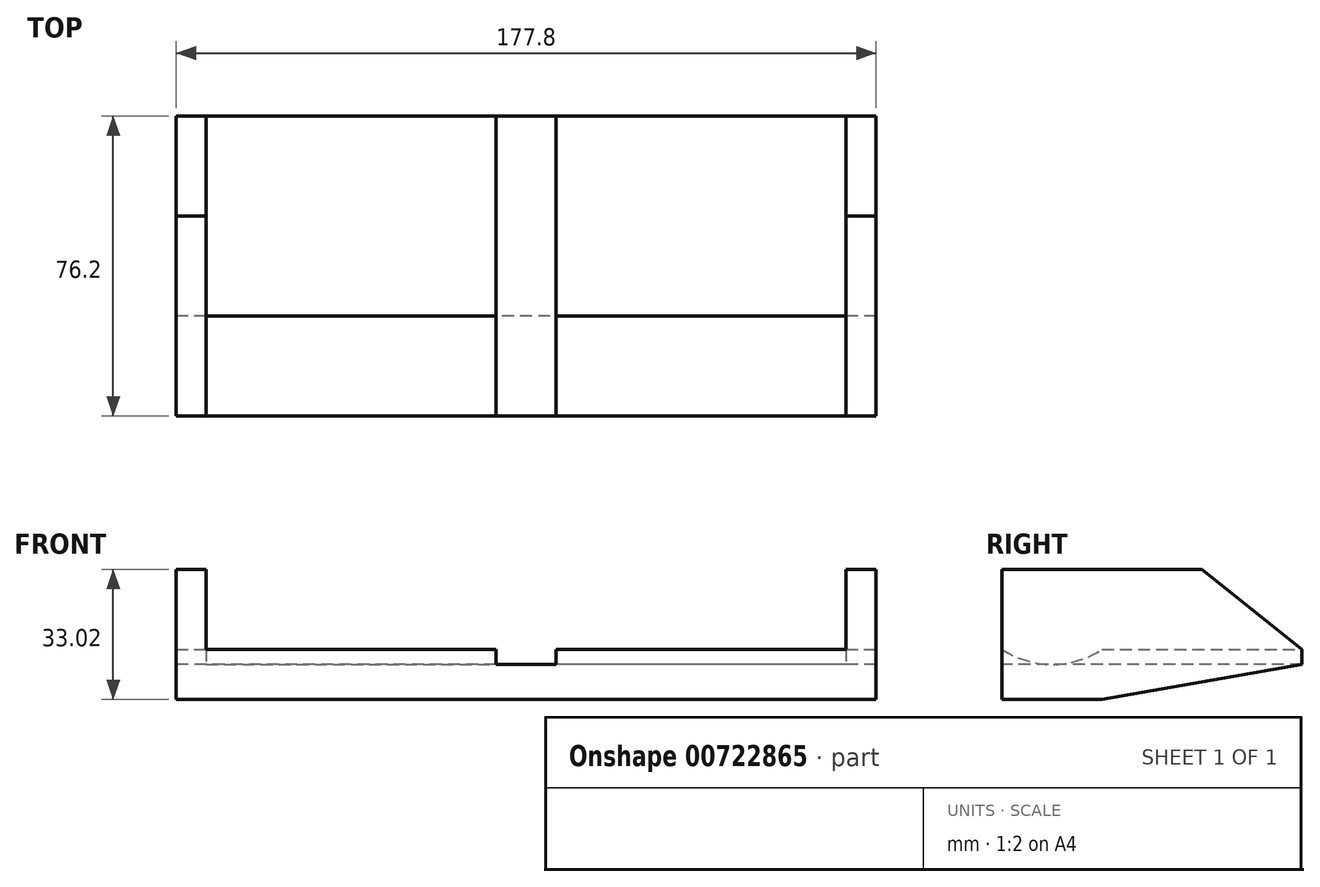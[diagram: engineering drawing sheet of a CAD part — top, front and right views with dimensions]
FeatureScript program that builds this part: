
annotation { "Feature Type Name" : "Feature", "Feature Type Description" : "" }
export const myFeature = defineFeature(function(context is Context, id is Id, definition is map)
    precondition{}
    {
        {
            var Q0;
            Q0=qCreatedBy(makeId("Top.planeOp"),FACE);
            var sketch = newSketch(context, id + "F0", { "sketchPlane" : qUnion([Q0])});
            skLineSegment(sketch, "E0.bottom", {"start": v(88.9, -38.1) * mm, "end": v(-88.9, -38.1) * mm});
            skLineSegment(sketch, "E0.top", {"start": v(88.9, 38.1) * mm, "end": v(-88.9, 38.1) * mm});
            skLineSegment(sketch, "E0.left", {"start": v(88.9, -38.1) * mm, "end": v(88.9, 38.1) * mm});
            skLineSegment(sketch, "E0.right", {"start": v(-88.9, -38.1) * mm, "end": v(-88.9, 38.1) * mm});
            skPoint(sketch, "E0.middle", {"position": v(0, 0) * mm});
            skSolve(sketch);
        }
        {
            var Q0;
            Q0=makeQuery(id+"F0.imprint","IMPRINT",FACE,{"disambiguationData":[TD([[makeQuery(id+"F0.imprint","IMPRINT",EDGE,{"derivedFrom":sQuery(id+"F0.wireOp",EDGE,"E0.bottom")}),-1.0]])]});
            extrude(context, id + "F1", {"entities" : qUnion([Q0]), "depth" : 12.7 * mm, "offsetDistance" : 25.4 * mm});
        }
        {
            var Q0;
            Q0=makeQuery(id+"F1.opExtrude","SWEPT_FACE",FACE,{"disambiguationData":[OSD([sQuery(id+"F0.wireOp",EDGE,"E0.bottom")])]});
            var sketch = newSketch(context, id + "F2", { "sketchPlane" : qUnion([Q0])});
            skLineSegment(sketch, "E1", {"start": v(0, 0) * mm, "end": v(0, 8.9) * mm});
            skLineSegment(sketch, "E2", {"start": v(0, 8.9) * mm, "end": v(7.62, 8.9) * mm});
            skLineSegment(sketch, "E3", {"start": v(7.62, 8.9) * mm, "end": v(-7.62, 8.9) * mm});
            skLineSegment(sketch, "E4", {"start": v(-7.62, 8.9) * mm, "end": v(-7.62, 12.7) * mm});
            skLineSegment(sketch, "E5", {"start": v(7.62, 8.9) * mm, "end": v(7.62, 12.7) * mm});
            skSolve(sketch);
        }
        {
            var Q0;
            {var subQ1=sQuery(id+"F2.wireOp",EDGE,"E4");Q0=makeQuery(id+"F2.imprint","IMPRINT",FACE,{"disambiguationData":[TD([[makeQuery(id+"F2.imprint","IMPRINT",EDGE,{"derivedFrom":subQ1}),-1.0]])]});}
            extrude(context, id + "F3", {"entities" : qUnion([Q0]), "operationType" : NewBodyOperationType.REMOVE, "oppositeDirection" : true, "depth" : 197.61 * mm, "offsetDistance" : 25.4 * mm});
        }
        {
            var Q0;
            {var subQ0=sQuery(id+"F0.wireOp",EDGE,"E0.bottom");var subQ1=sQuery(id+"F0.wireOp",EDGE,"E0.right");var subQ2=sQuery(id+"F0.wireOp",EDGE,"E0.top");Q0=makeQuery(id+"F3.boolean.opBoolean","SPLIT",FACE,{"disambiguationData":[TD([makeQuery(id+"F1.opExtrude","SWEPT_FACE",FACE,{"disambiguationData":[OSD([subQ1])]})])],"derivedFrom":makeQuery(id+"F1.opExtrude","CAP_FACE",FACE,{"disambiguationData":[OSD([subQ0,subQ2,sQuery(id+"F0.wireOp",EDGE,"E0.left"),subQ1])],"isStart":false})});}
            var sketch = newSketch(context, id + "F4", { "sketchPlane" : qUnion([Q0])});
            skLineSegment(sketch, "E6.bottom", {"start": v(-88.9, -38.1) * mm, "end": v(-81.28, -38.1) * mm});
            skLineSegment(sketch, "E6.top", {"start": v(-88.9, 38.1) * mm, "end": v(-81.28, 38.1) * mm});
            skLineSegment(sketch, "E6.left", {"start": v(-88.9, -38.1) * mm, "end": v(-88.9, 38.1) * mm});
            skLineSegment(sketch, "E6.right", {"start": v(-81.28, -38.1) * mm, "end": v(-81.28, 38.1) * mm});
            skSolve(sketch);
        }
        {
            var Q0;
            Q0=makeQuery(id+"F4.imprint","IMPRINT",FACE,{"disambiguationData":[TD([[makeQuery(id+"F4.imprint","IMPRINT",EDGE,{"derivedFrom":sQuery(id+"F4.wireOp",EDGE,"E6.bottom")}),-1.0]])]});
            extrude(context, id + "F5", {"entities" : qUnion([Q0]), "operationType" : NewBodyOperationType.ADD, "depth" : 20.32 * mm, "offsetDistance" : 25.4 * mm});
        }
        {
            var Q0;
            {var subQ0=sQuery(id+"F0.wireOp",EDGE,"E0.bottom");var subQ1=sQuery(id+"F0.wireOp",EDGE,"E0.top");var subQ2=sQuery(id+"F0.wireOp",EDGE,"E0.left");Q0=makeQuery(id+"F3.boolean.opBoolean","SPLIT",FACE,{"disambiguationData":[TD([makeQuery(id+"F1.opExtrude","SWEPT_FACE",FACE,{"disambiguationData":[OSD([subQ2])]})])],"derivedFrom":makeQuery(id+"F1.opExtrude","CAP_FACE",FACE,{"disambiguationData":[OSD([subQ0,subQ1,subQ2,sQuery(id+"F0.wireOp",EDGE,"E0.right")])],"isStart":false})});}
            var sketch = newSketch(context, id + "F6", { "sketchPlane" : qUnion([Q0])});
            skLineSegment(sketch, "E7.bottom", {"start": v(88.9, -38.1) * mm, "end": v(81.28, -38.1) * mm});
            skLineSegment(sketch, "E7.top", {"start": v(88.9, 38.1) * mm, "end": v(81.28, 38.1) * mm});
            skLineSegment(sketch, "E7.left", {"start": v(88.9, -38.1) * mm, "end": v(88.9, 38.1) * mm});
            skLineSegment(sketch, "E7.right", {"start": v(81.28, -38.1) * mm, "end": v(81.28, 38.1) * mm});
            skSolve(sketch);
        }
        {
            var Q0;
            Q0=makeQuery(id+"F6.imprint","IMPRINT",FACE,{"disambiguationData":[TD([[makeQuery(id+"F6.imprint","IMPRINT",EDGE,{"derivedFrom":sQuery(id+"F6.wireOp",EDGE,"E7.bottom")}),-1.0]])]});
            extrude(context, id + "F7", {"entities" : qUnion([Q0]), "operationType" : NewBodyOperationType.ADD, "depth" : 20.32 * mm, "offsetDistance" : 25.4 * mm});
        }
        {
            var Q0;
            Q0=makeQuery(id+"F3.boolean.opBoolean","COPY",FACE,{"derivedFrom":makeQuery(id+"F3.opExtrude","SWEPT_FACE",FACE,{"disambiguationData":[OSD([sQuery(id+"F2.wireOp",EDGE,"E4")])]})});
            var sketch = newSketch(context, id + "F8", { "sketchPlane" : qUnion([Q0])});
            skLineSegment(sketch, "E8", {"start": v(-38.1, 12.7) * mm, "end": v(-12.7, 12.7) * mm});
            skArc(sketch, "E9", {"start": v(-38.1, 12.7) * mm, "mid": v(-25.4, 8.9) * mm, "end": v(-12.7, 12.7) * mm});
            skSolve(sketch);
        }
        {
            var Q0;
            {var subQ0=sQuery(id+"F8.wireOp",EDGE,"E8");Q0=makeQuery(id+"F8.imprint","IMPRINT",FACE,{"disambiguationData":[TD([[makeQuery(id+"F8.imprint","IMPRINT",EDGE,{"derivedFrom":subQ0}),1.0]])]});}
            extrude(context, id + "F9", {"entities" : qUnion([Q0]), "operationType" : NewBodyOperationType.REMOVE, "oppositeDirection" : true, "depth" : 73.66 * mm, "offsetDistance" : 25.4 * mm});
        }
        {
            var Q0;
            Q0=makeQuery(id+"F3.boolean.opBoolean","COPY",FACE,{"derivedFrom":makeQuery(id+"F3.opExtrude","SWEPT_FACE",FACE,{"disambiguationData":[OSD([sQuery(id+"F2.wireOp",EDGE,"E5")])]})});
            var sketch = newSketch(context, id + "F10", { "sketchPlane" : qUnion([Q0])});
            skLineSegment(sketch, "E10", {"start": v(38.1, 12.7) * mm, "end": v(12.7, 12.7) * mm});
            skArc(sketch, "E11", {"start": v(12.7, 12.7) * mm, "mid": v(25.4, 8.9) * mm, "end": v(38.1, 12.7) * mm});
            skSolve(sketch);
        }
        {
            var Q0;
            Q0=makeQuery(id+"F10.imprint","IMPRINT",FACE,{"disambiguationData":[TD([[makeQuery(id+"F10.imprint","IMPRINT",EDGE,{"derivedFrom":sQuery(id+"F10.wireOp",EDGE,"E10")}),-1.0]])]});
            extrude(context, id + "F11", {"entities" : qUnion([Q0]), "operationType" : NewBodyOperationType.REMOVE, "oppositeDirection" : true, "depth" : 73.66 * mm, "offsetDistance" : 25.4 * mm});
        }
        {
            var Q0;
            Q0=makeQuery(id+"F5.boolean.opBoolean","MERGE",FACE,{"derivedFrom":[makeQuery(id+"F1.opExtrude","SWEPT_FACE",FACE,{"disambiguationData":[OSD([sQuery(id+"F0.wireOp",EDGE,"E0.right")])]}),makeQuery(id+"F5.opExtrude","SWEPT_FACE",FACE,{"disambiguationData":[OSD([sQuery(id+"F4.wireOp",EDGE,"E6.left")])]})]});
            var sketch = newSketch(context, id + "F12", { "sketchPlane" : qUnion([Q0])});
            skLineSegment(sketch, "E12", {"start": v(38.1, 0) * mm, "end": v(12.7, 0) * mm});
            skLineSegment(sketch, "E13", {"start": v(-38.1, 0) * mm, "end": v(-38.1, 8.9) * mm});
            skLineSegment(sketch, "E14", {"start": v(-38.1, 8.9) * mm, "end": v(12.7, 0) * mm});
            skSolve(sketch);
        }
        {
            var Q0;
            {var subQ0=sQuery(id+"F12.wireOp",EDGE,"E13");Q0=makeQuery(id+"F12.imprint","IMPRINT",FACE,{"disambiguationData":[TD([[makeQuery(id+"F12.imprint","IMPRINT",EDGE,{"derivedFrom":subQ0}),1.0]])]});}
            extrude(context, id + "F13", {"entities" : qUnion([Q0]), "operationType" : NewBodyOperationType.REMOVE, "oppositeDirection" : true, "depth" : 228.6 * mm, "offsetDistance" : 25.4 * mm});
        }
        {
            var Q0;
            Q0=makeQuery(id+"F7.boolean.opBoolean","MERGE",FACE,{"derivedFrom":[makeQuery(id+"F1.opExtrude","SWEPT_FACE",FACE,{"disambiguationData":[OSD([sQuery(id+"F0.wireOp",EDGE,"E0.left")])]}),makeQuery(id+"F7.opExtrude","SWEPT_FACE",FACE,{"disambiguationData":[OSD([sQuery(id+"F6.wireOp",EDGE,"E7.left")])]})]});
            var sketch = newSketch(context, id + "F14", { "sketchPlane" : qUnion([Q0])});
            skLineSegment(sketch, "E15", {"start": v(-38.1, 33.02) * mm, "end": v(12.7, 33.02) * mm});
            skLineSegment(sketch, "E16", {"start": v(38.1, 33.02) * mm, "end": v(38.1, 12.7) * mm});
            skLineSegment(sketch, "E17", {"start": v(38.1, 12.7) * mm, "end": v(12.7, 33.02) * mm});
            skSolve(sketch);
        }
        {
            var Q0;
            {var subQ0=sQuery(id+"F14.wireOp",EDGE,"E16");Q0=makeQuery(id+"F14.imprint","IMPRINT",FACE,{"disambiguationData":[TD([[makeQuery(id+"F14.imprint","IMPRINT",EDGE,{"derivedFrom":subQ0}),-1.0]])]});}
            extrude(context, id + "F15", {"entities" : qUnion([Q0]), "operationType" : NewBodyOperationType.REMOVE, "oppositeDirection" : true, "depth" : 228.6 * mm, "offsetDistance" : 25.4 * mm});
        }
    });
